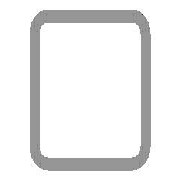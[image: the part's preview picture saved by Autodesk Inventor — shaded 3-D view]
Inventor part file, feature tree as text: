
AUTODESK INVENTOR PART (.ipt)
format: ipt  version: 2025 (Build 290162010, 162A)  size: 134,656 bytes
history: native  units: mm (DEFAULTED — no unit token found)
features: other x4, sketch x1, plane x1
ambient origin geometry x8: Origin, YZ Plane, XZ Plane, XY Plane, X Axis, Y Axis, Z Axis, Center Point
bodies: Solid1 (feature_tree), Body (feature_tree)
feature tree (6):
  parser-record x1  (decoder bookkeeping rows leaked as tree rows — omitted from the tree; the rows remain in map.json)
  other  "Driven Length"
  other  "Start Plane"
  other  "End Plane"
  sketch  "Sketch3"  dims[d3=1580.0mm d4=0.0mm d7=6.0mm d9=80.0mm d11=80.0mm d12=3.0mm d13=40.0mm d14=1620.0mm d15=40.0mm d16=40.0mm d17=90.0deg d18=1580.0mm]
  plane  "Work Plane3"
